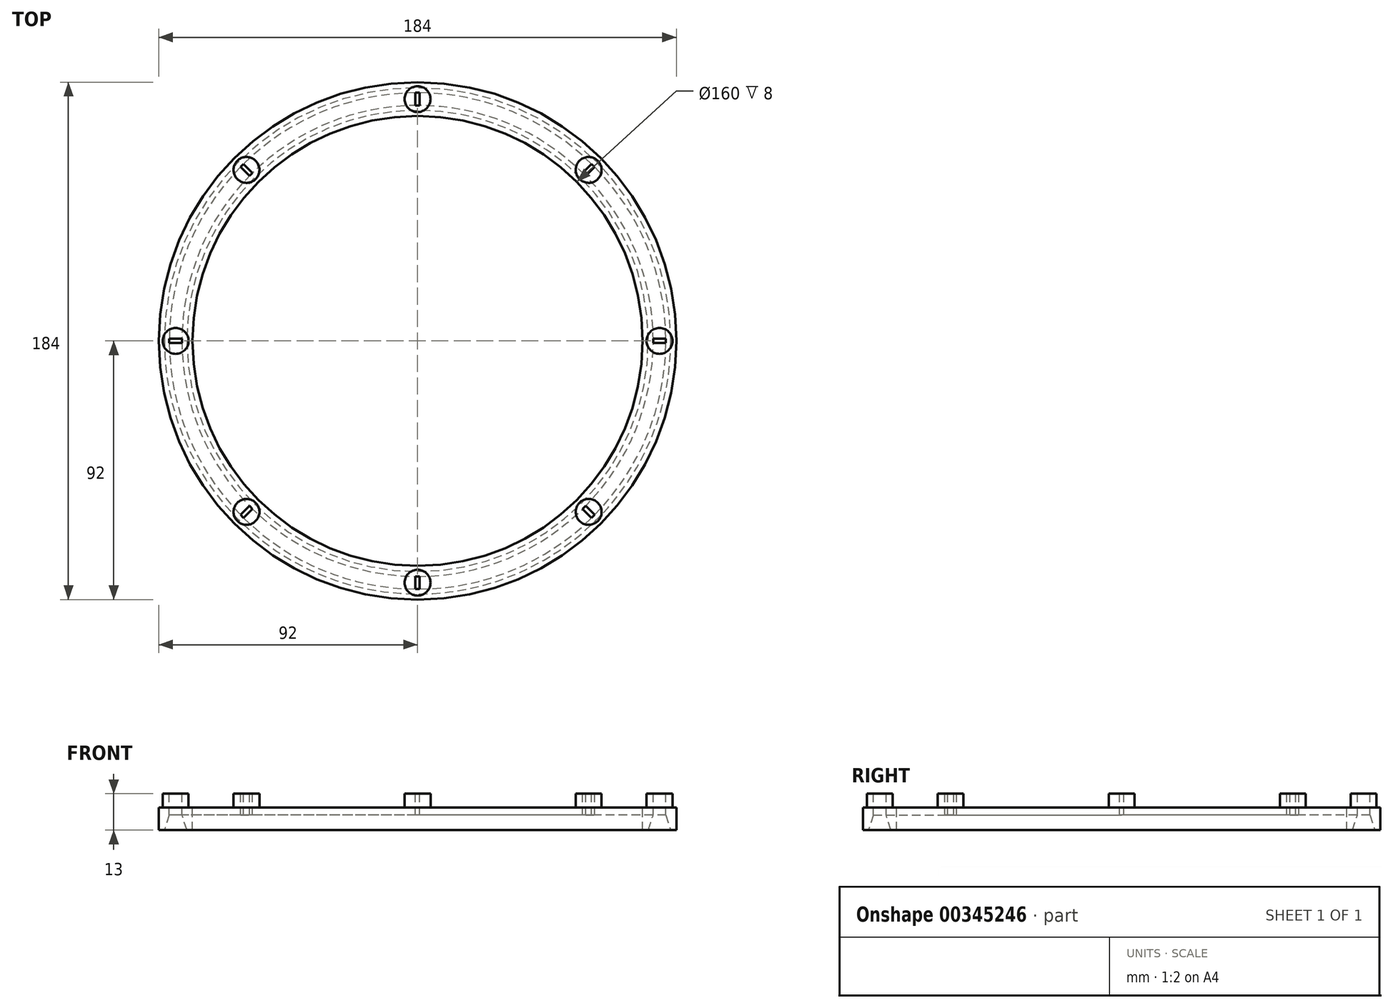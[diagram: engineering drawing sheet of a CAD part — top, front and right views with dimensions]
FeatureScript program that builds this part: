
annotation { "Feature Type Name" : "Feature", "Feature Type Description" : "" }
export const myFeature = defineFeature(function(context is Context, id is Id, definition is map)
    precondition{}
    {
        {
            var Q0;
            Q0=qCreatedBy(makeId("Front.planeOp"),FACE);
            var sketch = newSketch(context, id + "F0", { "sketchPlane" : qUnion([Q0])});
            skLineSegment(sketch, "E0", {"start": v(80, 3.42) * mm, "end": v(80, -4.58) * mm});
            skLineSegment(sketch, "E1", {"start": v(80, 3.42) * mm, "end": v(86, 3.42) * mm});
            skLineSegment(sketch, "E2", {"start": v(80, -4.58) * mm, "end": v(82, -4.58) * mm});
            skLineSegment(sketch, "E3", {"start": v(82, -4.58) * mm, "end": v(83.75, 0.82) * mm});
            skLineSegment(sketch, "E4", {"start": v(86, 9.43) * mm, "end": v(86, -10.3) * mm, "construction": true});
            skLineSegment(sketch, "E5", {"start": v(83.75, 0.82) * mm, "end": v(86, 0.82) * mm});
            skLineSegment(sketch, "E6.MirrorCS", {"start": v(92, -4.58) * mm, "end": v(90, -4.58) * mm});
            skLineSegment(sketch, "E7.MirrorCS", {"start": v(92, 3.42) * mm, "end": v(92, -4.58) * mm});
            skLineSegment(sketch, "E8.MirrorCS", {"start": v(90, -4.58) * mm, "end": v(88.25, 0.82) * mm});
            skLineSegment(sketch, "E9.MirrorCS", {"start": v(88.25, 0.82) * mm, "end": v(86, 0.82) * mm});
            skLineSegment(sketch, "E10.MirrorCS", {"start": v(92, 3.42) * mm, "end": v(86, 3.42) * mm});
            skSolve(sketch);
        }
        {
            var Q0;
            Q0=qCreatedBy(makeId("Right.planeOp"),FACE);
            var sketch = newSketch(context, id + "F1", { "sketchPlane" : qUnion([Q0])});
            skLineSegment(sketch, "E11", {"start": v(0, 18.9) * mm, "end": v(0, -24.11) * mm, "construction": true});
            skSolve(sketch);
        }
        {
            var Q0;
            Q0 = qSketchRegion(id + "F0", true);
            var Q1;
            Q1=sQuery(id+"F1.wireOp",EDGE,"E11");
            revolve(context, id + "F2", {"entities" : qUnion([Q0]), "axis" : qUnion([Q1]), "revolveType" : RevolveType.FULL});
        }
        {
            var Q0;
            Q0=makeQuery(id+"F2.opRevolve","SWEPT_FACE",FACE,{"disambiguationData":[OSD([sQuery(id+"F0.wireOp",EDGE,"E1"),sQuery(id+"F0.wireOp",EDGE,"E10.MirrorCS")])]});
            var sketch = newSketch(context, id + "F3", { "sketchPlane" : qUnion([Q0])});
            skCircle(sketch, "E12", {"center": v(-86, 0) * mm, "radius": 4.6 * mm});
            skLineSegment(sketch, "E13", {"start": v(-92, 0) * mm, "end": v(-80, 0) * mm, "construction": true});
            skLineSegment(sketch, "E14", {"start": v(-88.25, 0) * mm, "end": v(-88.25, 0.75) * mm});
            skLineSegment(sketch, "E15", {"start": v(-88.25, 0.75) * mm, "end": v(-86, 0.75) * mm});
            skLineSegment(sketch, "E16", {"start": v(-86, 3.42) * mm, "end": v(-86, -4.05) * mm, "construction": true});
            skLineSegment(sketch, "E17.MirrorCS", {"start": v(-88.25, -0.75) * mm, "end": v(-86, -0.75) * mm});
            skLineSegment(sketch, "E18.MirrorCS", {"start": v(-88.25, 0) * mm, "end": v(-88.25, -0.75) * mm});
            skLineSegment(sketch, "E19.MirrorCS", {"start": v(-83.75, 0.75) * mm, "end": v(-86, 0.75) * mm});
            skLineSegment(sketch, "E20.MirrorCS", {"start": v(-83.75, 0) * mm, "end": v(-83.75, 0.75) * mm});
            skLineSegment(sketch, "E21.MirrorCS", {"start": v(-83.75, 0) * mm, "end": v(-83.75, -0.75) * mm});
            skLineSegment(sketch, "E22.MirrorCS", {"start": v(-83.75, -0.75) * mm, "end": v(-86, -0.75) * mm});
            skSolve(sketch);
        }
        {
            var Q0;
            Q0=makeQuery(id+"F3.imprint","IMPRINT",FACE,{"disambiguationData":[TD([[makeQuery(id+"F3.imprint","IMPRINT",EDGE,{"derivedFrom":sQuery(id+"F3.wireOp",EDGE,"E12")}),1.0]])]});
            extrude(context, id + "F4", {"entities" : qUnion([Q0]), "depth" : 5 * mm});
        }
        {
            var Q0;
            Q0=makeQuery(id+"F3.imprint","IMPRINT",FACE,{"disambiguationData":[TD([[makeQuery(id+"F3.imprint","IMPRINT",EDGE,{"derivedFrom":sQuery(id+"F3.wireOp",EDGE,"E14")}),-1.0]])]});
            extrude(context, id + "F5", {"entities" : qUnion([Q0]), "oppositeDirection" : true, "depth" : 25 * mm});
        }
        {
            var Q0;
            Q0=makeQuery(id+"F5.opExtrude","SWEPT_BODY",BODY,{"disambiguationData":[OSD([sQuery(id+"F3.wireOp",EDGE,"E14"),sQuery(id+"F3.wireOp",EDGE,"E15"),sQuery(id+"F3.wireOp",EDGE,"E17.MirrorCS"),sQuery(id+"F3.wireOp",EDGE,"E18.MirrorCS"),sQuery(id+"F3.wireOp",EDGE,"E19.MirrorCS"),sQuery(id+"F3.wireOp",EDGE,"E20.MirrorCS"),sQuery(id+"F3.wireOp",EDGE,"E21.MirrorCS"),sQuery(id+"F3.wireOp",EDGE,"E22.MirrorCS")])]});
            var Q1;
            Q1=sQuery(id+"F1.wireOp",EDGE,"E11");
            circularPattern(context, id + "F6", {"operationType" : NewBodyOperationType.REMOVE, "entities" : qUnion([Q0]), "axis" : qUnion([Q1]), "angle" : 360 * degree, "instanceCount" : 8, "equalSpace" : true});
        }
        {
            var Q0;
            Q0=makeQuery(id+"F4.opExtrude","SWEPT_BODY",BODY,{"disambiguationData":[OSD([sQuery(id+"F3.wireOp",EDGE,"E12"),sQuery(id+"F3.wireOp",EDGE,"E14"),sQuery(id+"F3.wireOp",EDGE,"E15"),sQuery(id+"F3.wireOp",EDGE,"E17.MirrorCS"),sQuery(id+"F3.wireOp",EDGE,"E18.MirrorCS"),sQuery(id+"F3.wireOp",EDGE,"E19.MirrorCS"),sQuery(id+"F3.wireOp",EDGE,"E20.MirrorCS"),sQuery(id+"F3.wireOp",EDGE,"E21.MirrorCS"),sQuery(id+"F3.wireOp",EDGE,"E22.MirrorCS")])]});
            var Q1;
            Q1=sQuery(id+"F1.wireOp",EDGE,"E11");
            var Q2;
            Q2=makeQuery(id+"F4.opExtrude","SWEPT_BODY",BODY,{"disambiguationData":[OSD([sQuery(id+"F3.wireOp",EDGE,"E12"),sQuery(id+"F3.wireOp",EDGE,"E14"),sQuery(id+"F3.wireOp",EDGE,"E15"),sQuery(id+"F3.wireOp",EDGE,"E17.MirrorCS"),sQuery(id+"F3.wireOp",EDGE,"E18.MirrorCS"),sQuery(id+"F3.wireOp",EDGE,"E19.MirrorCS"),sQuery(id+"F3.wireOp",EDGE,"E20.MirrorCS"),sQuery(id+"F3.wireOp",EDGE,"E21.MirrorCS"),sQuery(id+"F3.wireOp",EDGE,"E22.MirrorCS")])]});
            circularPattern(context, id + "F7", {"operationType" : NewBodyOperationType.ADD, "entities" : qUnion([Q0]), "axis" : qUnion([Q1]), "angle" : 360 * degree, "instanceCount" : 8, "equalSpace" : true});
        }
    });
